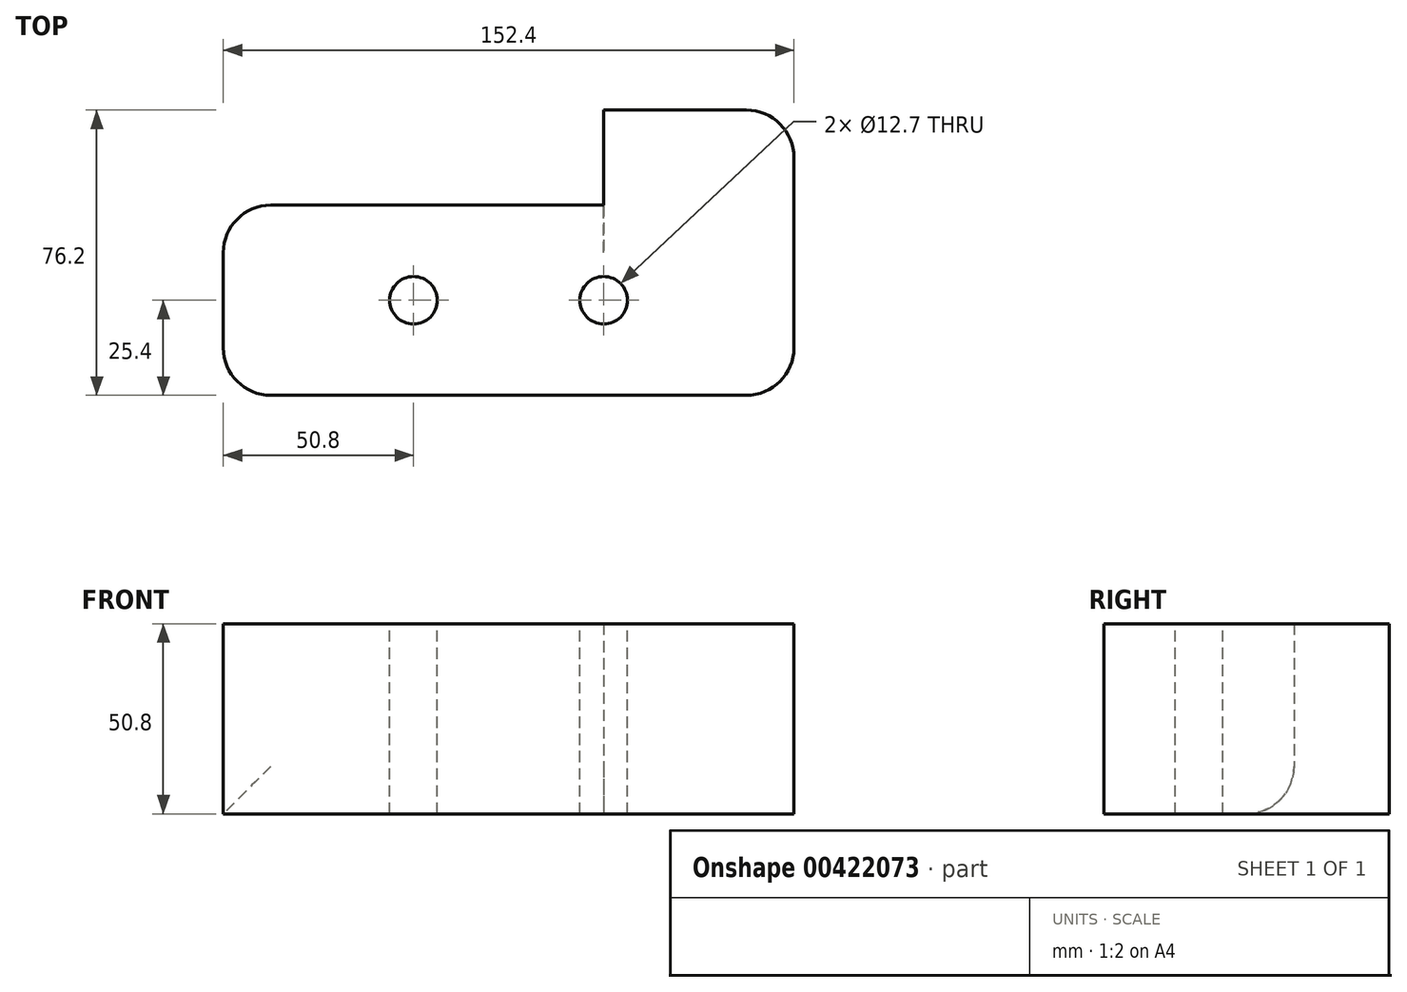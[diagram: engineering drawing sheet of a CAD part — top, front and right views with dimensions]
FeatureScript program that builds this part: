
annotation { "Feature Type Name" : "Feature", "Feature Type Description" : "" }
export const myFeature = defineFeature(function(context is Context, id is Id, definition is map)
    precondition{}
    {
        {
            var Q0;
            Q0=qCreatedBy(makeId("Top.planeOp"),FACE);
            var sketch = newSketch(context, id + "F0", { "sketchPlane" : qUnion([Q0])});
            skLineSegment(sketch, "E0", {"start": v(0, 0) * mm, "end": v(152.4, 0) * mm});
            skLineSegment(sketch, "E1", {"start": v(0, 0) * mm, "end": v(0, 50.8) * mm});
            skLineSegment(sketch, "E2", {"start": v(0, 50.8) * mm, "end": v(101.6, 50.8) * mm});
            skLineSegment(sketch, "E3", {"start": v(101.6, 50.8) * mm, "end": v(101.6, 76.2) * mm});
            skLineSegment(sketch, "E4", {"start": v(101.6, 76.2) * mm, "end": v(152.4, 76.2) * mm});
            skLineSegment(sketch, "E5", {"start": v(152.4, 76.2) * mm, "end": v(152.4, 0) * mm});
            skSolve(sketch);
        }
        {
            var Q0;
            Q0=makeQuery(id+"F0.imprint","IMPRINT",FACE,{"disambiguationData":[TD([[makeQuery(id+"F0.imprint","IMPRINT",EDGE,{"derivedFrom":sQuery(id+"F0.wireOp",EDGE,"E0")}),1.0]])]});
            extrude(context, id + "F1", {"entities" : qUnion([Q0]), "depth" : 50.8 * mm});
        }
        {
            var Q0;
            Q0=makeQuery(id+"F1.opExtrude","SWEPT_EDGE",EDGE,{"disambiguationData":[OSD([sQuery(id+"F0.wireOp",EDGE,"E4"),sQuery(id+"F0.wireOp",EDGE,"E5")])]});
            var Q1;
            Q1=makeQuery(id+"F1.opExtrude","SWEPT_EDGE",EDGE,{"disambiguationData":[OSD([sQuery(id+"F0.wireOp",EDGE,"E0"),sQuery(id+"F0.wireOp",EDGE,"E5")])]});
            var Q2;
            Q2=makeQuery(id+"F1.opExtrude","CAP_EDGE",EDGE,{"disambiguationData":[OSD([sQuery(id+"F0.wireOp",EDGE,"E2")])],"isStart":true});
            var Q3;
            Q3=makeQuery(id+"F1.opExtrude","SWEPT_EDGE",EDGE,{"disambiguationData":[OSD([sQuery(id+"F0.wireOp",EDGE,"E1"),sQuery(id+"F0.wireOp",EDGE,"E2")])]});
            var Q4;
            Q4=makeQuery(id+"F1.opExtrude","SWEPT_EDGE",EDGE,{"disambiguationData":[OSD([sQuery(id+"F0.wireOp",EDGE,"E0"),sQuery(id+"F0.wireOp",EDGE,"E1")])]});
            fillet(context, id + "F2", {"entities" : qUnion([Q0, Q1, Q2, Q3, Q4]), "radius" : 12.7 * mm, "tangentPropagation" : true, "allowEdgeOverflow" : false});
        }
        {
            var Q0;
            Q0=makeQuery(id+"F1.opExtrude","CAP_FACE",FACE,{"disambiguationData":[OSD([sQuery(id+"F0.wireOp",EDGE,"E0"),sQuery(id+"F0.wireOp",EDGE,"E1"),sQuery(id+"F0.wireOp",EDGE,"E2"),sQuery(id+"F0.wireOp",EDGE,"E3"),sQuery(id+"F0.wireOp",EDGE,"E4"),sQuery(id+"F0.wireOp",EDGE,"E5")])],"isStart":false});
            var sketch = newSketch(context, id + "F3", { "sketchPlane" : qUnion([Q0])});
            skPoint(sketch, "E6", {"position": v(50.8, 25.4) * mm});
            skPoint(sketch, "E6.positionSnap0", {"position": v(0, 25.4) * mm});
            skPoint(sketch, "E7", {"position": v(101.6, 25.4) * mm});
            skSolve(sketch);
        }
        {
            var Q0;
            Q0=sQuery(id+"F3.wireOp",VERTEX,"E6");
            var Q1;
            Q1=sQuery(id+"F3.wireOp",VERTEX,"E7");
            var Q2;
            Q2=makeQuery(id+"F1.opExtrude","SWEPT_BODY",BODY,{"disambiguationData":[OSD([sQuery(id+"F0.wireOp",EDGE,"E0"),sQuery(id+"F0.wireOp",EDGE,"E1"),sQuery(id+"F0.wireOp",EDGE,"E2"),sQuery(id+"F0.wireOp",EDGE,"E3"),sQuery(id+"F0.wireOp",EDGE,"E4"),sQuery(id+"F0.wireOp",EDGE,"E5")])]});
            hole(context, id + "F4", {"style" : HoleStyle.SIMPLE, "endStyle" : HoleEndStyle.THROUGH, "holeDiameter" : 12.7 * mm, "isTappedThrough" : true, "tappedDepth" : 12.7 * mm, "tapClearance" : 3, "locations" : qUnion([Q0, Q1]), "scope" : qUnion([Q2])});
        }
    });
